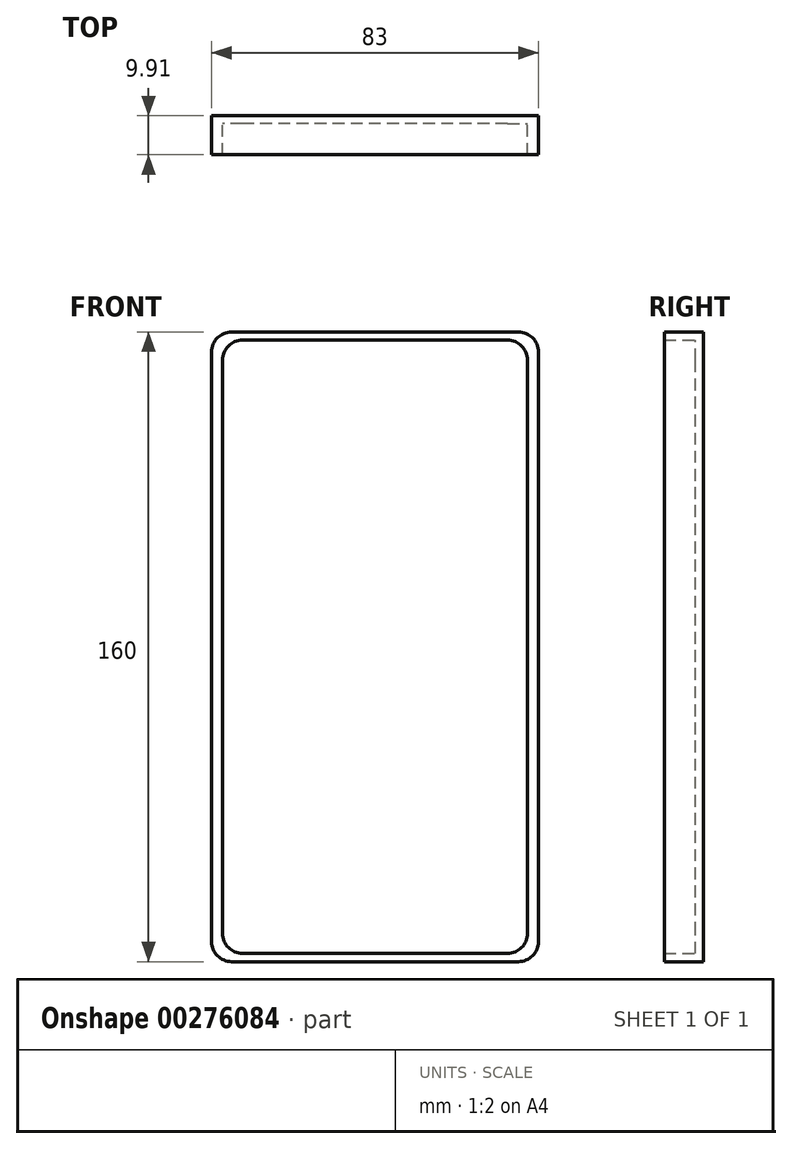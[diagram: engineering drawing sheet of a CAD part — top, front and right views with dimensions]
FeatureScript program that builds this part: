
annotation { "Feature Type Name" : "Feature", "Feature Type Description" : "" }
export const myFeature = defineFeature(function(context is Context, id is Id, definition is map)
    precondition{}
    {
        {
            var Q0;
            Q0=qCreatedBy(makeId("Front.planeOp"),FACE);
            var sketch = newSketch(context, id + "F0", { "sketchPlane" : qUnion([Q0])});
            skLineSegment(sketch, "E0.bottom", {"start": v(41.5, -80) * mm, "end": v(-41.5, -80) * mm});
            skLineSegment(sketch, "E0.top", {"start": v(41.5, 80) * mm, "end": v(-41.5, 80) * mm});
            skLineSegment(sketch, "E0.left", {"start": v(41.5, -80) * mm, "end": v(41.5, 80) * mm});
            skLineSegment(sketch, "E0.right", {"start": v(-41.5, -80) * mm, "end": v(-41.5, 80) * mm});
            skPoint(sketch, "E0.middle", {"position": v(0, 0) * mm});
            skLineSegment(sketch, "E1.bottom", {"start": v(38.73, -77.91) * mm, "end": v(-38.73, -77.91) * mm});
            skLineSegment(sketch, "E1.top", {"start": v(38.73, 77.91) * mm, "end": v(-38.73, 77.91) * mm});
            skLineSegment(sketch, "E1.left", {"start": v(38.73, -77.91) * mm, "end": v(38.73, 77.91) * mm});
            skLineSegment(sketch, "E1.right", {"start": v(-38.73, -77.91) * mm, "end": v(-38.73, 77.91) * mm});
            skSolve(sketch);
        }
        {
            var Q0;
            Q0=makeQuery(id+"F0.imprint","IMPRINT",FACE,{"disambiguationData":[TD([[makeQuery(id+"F0.imprint","IMPRINT",EDGE,{"derivedFrom":sQuery(id+"F0.wireOp",EDGE,"E0.bottom")}),-1.0]])]});
            extrude(context, id + "F1", {"entities" : qUnion([Q0]), "depth" : 9.9 * mm});
        }
        {
            var Q0;
            Q0=makeQuery(id+"F0.imprint","IMPRINT",FACE,{"disambiguationData":[TD([[makeQuery(id+"F0.imprint","IMPRINT",EDGE,{"derivedFrom":sQuery(id+"F0.wireOp",EDGE,"E1.bottom")}),-1.0]])]});
            extrude(context, id + "F2", {"entities" : qUnion([Q0]), "operationType" : NewBodyOperationType.ADD, "depth" : 2 * mm});
        }
        {
            var Q0;
            Q0=makeQuery(id+"F1.opExtrude","SWEPT_EDGE",EDGE,{"disambiguationData":[OSD([sQuery(id+"F0.wireOp",EDGE,"E1.top"),sQuery(id+"F0.wireOp",EDGE,"E1.right")])]});
            var Q1;
            Q1=makeQuery(id+"F1.opExtrude","SWEPT_EDGE",EDGE,{"disambiguationData":[OSD([sQuery(id+"F0.wireOp",EDGE,"E1.top"),sQuery(id+"F0.wireOp",EDGE,"E1.left")])]});
            var Q2;
            Q2=makeQuery(id+"F1.opExtrude","SWEPT_EDGE",EDGE,{"disambiguationData":[OSD([sQuery(id+"F0.wireOp",EDGE,"E1.bottom"),sQuery(id+"F0.wireOp",EDGE,"E1.right")])]});
            var Q3;
            Q3=makeQuery(id+"F1.opExtrude","SWEPT_EDGE",EDGE,{"disambiguationData":[OSD([sQuery(id+"F0.wireOp",EDGE,"E1.bottom"),sQuery(id+"F0.wireOp",EDGE,"E1.left")])]});
            var Q4;
            Q4=makeQuery(id+"F1.opExtrude","SWEPT_EDGE",EDGE,{"disambiguationData":[OSD([sQuery(id+"F0.wireOp",EDGE,"E0.bottom"),sQuery(id+"F0.wireOp",EDGE,"E0.left")])]});
            var Q5;
            Q5=makeQuery(id+"F1.opExtrude","SWEPT_EDGE",EDGE,{"disambiguationData":[OSD([sQuery(id+"F0.wireOp",EDGE,"E0.top"),sQuery(id+"F0.wireOp",EDGE,"E0.right")])]});
            var Q6;
            Q6=makeQuery(id+"F1.opExtrude","SWEPT_EDGE",EDGE,{"disambiguationData":[OSD([sQuery(id+"F0.wireOp",EDGE,"E0.bottom"),sQuery(id+"F0.wireOp",EDGE,"E0.right")])]});
            var Q7;
            Q7=makeQuery(id+"F1.opExtrude","SWEPT_EDGE",EDGE,{"disambiguationData":[OSD([sQuery(id+"F0.wireOp",EDGE,"E0.top"),sQuery(id+"F0.wireOp",EDGE,"E0.left")])]});
            fillet(context, id + "F3", {"entities" : qUnion([Q0, Q1, Q2, Q3, Q4, Q5, Q6, Q7]), "radius" : 5.08 * mm, "tangentPropagation" : true, "allowEdgeOverflow" : false});
        }
    });
